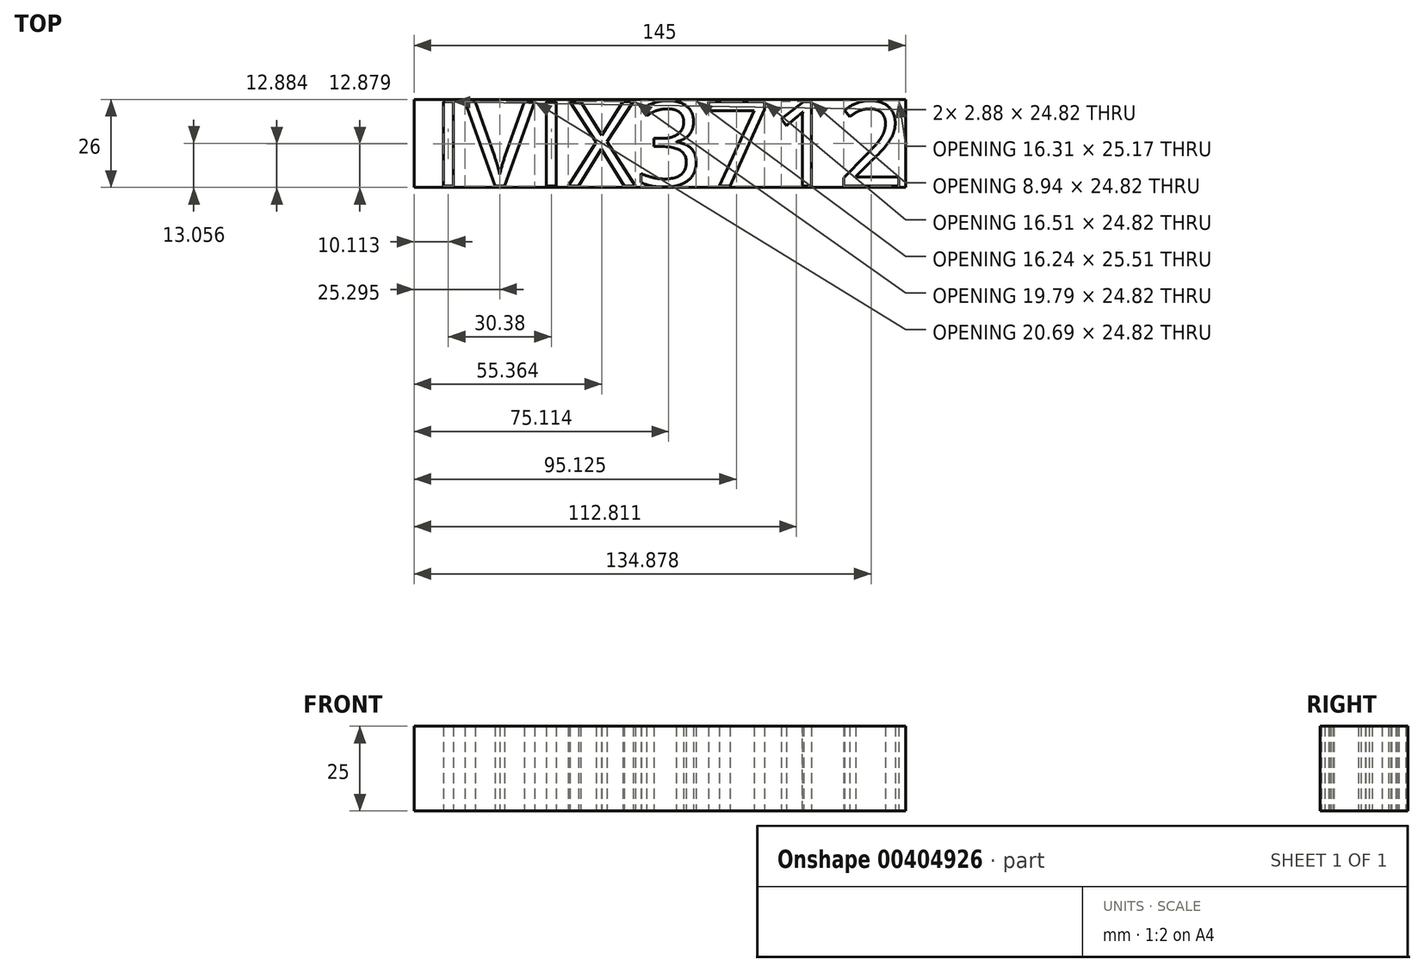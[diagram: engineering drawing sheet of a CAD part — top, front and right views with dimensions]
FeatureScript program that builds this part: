
annotation { "Feature Type Name" : "Feature", "Feature Type Description" : "" }
export const myFeature = defineFeature(function(context is Context, id is Id, definition is map)
    precondition{}
    {
        {
            var Q0;
            Q0=qCreatedBy(makeId("Top.planeOp"),FACE);
            var sketch = newSketch(context, id + "F0", { "sketchPlane" : qUnion([Q0])});
            skText(sketch, "E0", { "text": "IVIX3712", "fontName": "OpenSans-Regular.ttf"});
            skLineSegment(sketch, "E1.bottom", {"start": v(-59.28, 26) * mm, "end": v(85.72, 26) * mm});
            skLineSegment(sketch, "E1.top", {"start": v(-59.28, 0) * mm, "end": v(85.72, 0) * mm});
            skLineSegment(sketch, "E1.left", {"start": v(-59.28, 26) * mm, "end": v(-59.28, 0) * mm});
            skLineSegment(sketch, "E1.right", {"start": v(85.72, 26) * mm, "end": v(85.72, 0) * mm});
            const initialGuessF0  = {"E0": [-0.05402, 0.00047, 1, 0, 0.02503]};
            skSetInitialGuess(sketch, initialGuessF0);
            skSolve(sketch);
        }
        {
            var Q0;
            Q0 = qSketchRegion(id + "F0", true);
            extrude(context, id + "F1", {"entities" : qUnion([Q0]), "depth" : 25 * mm});
        }
    });
